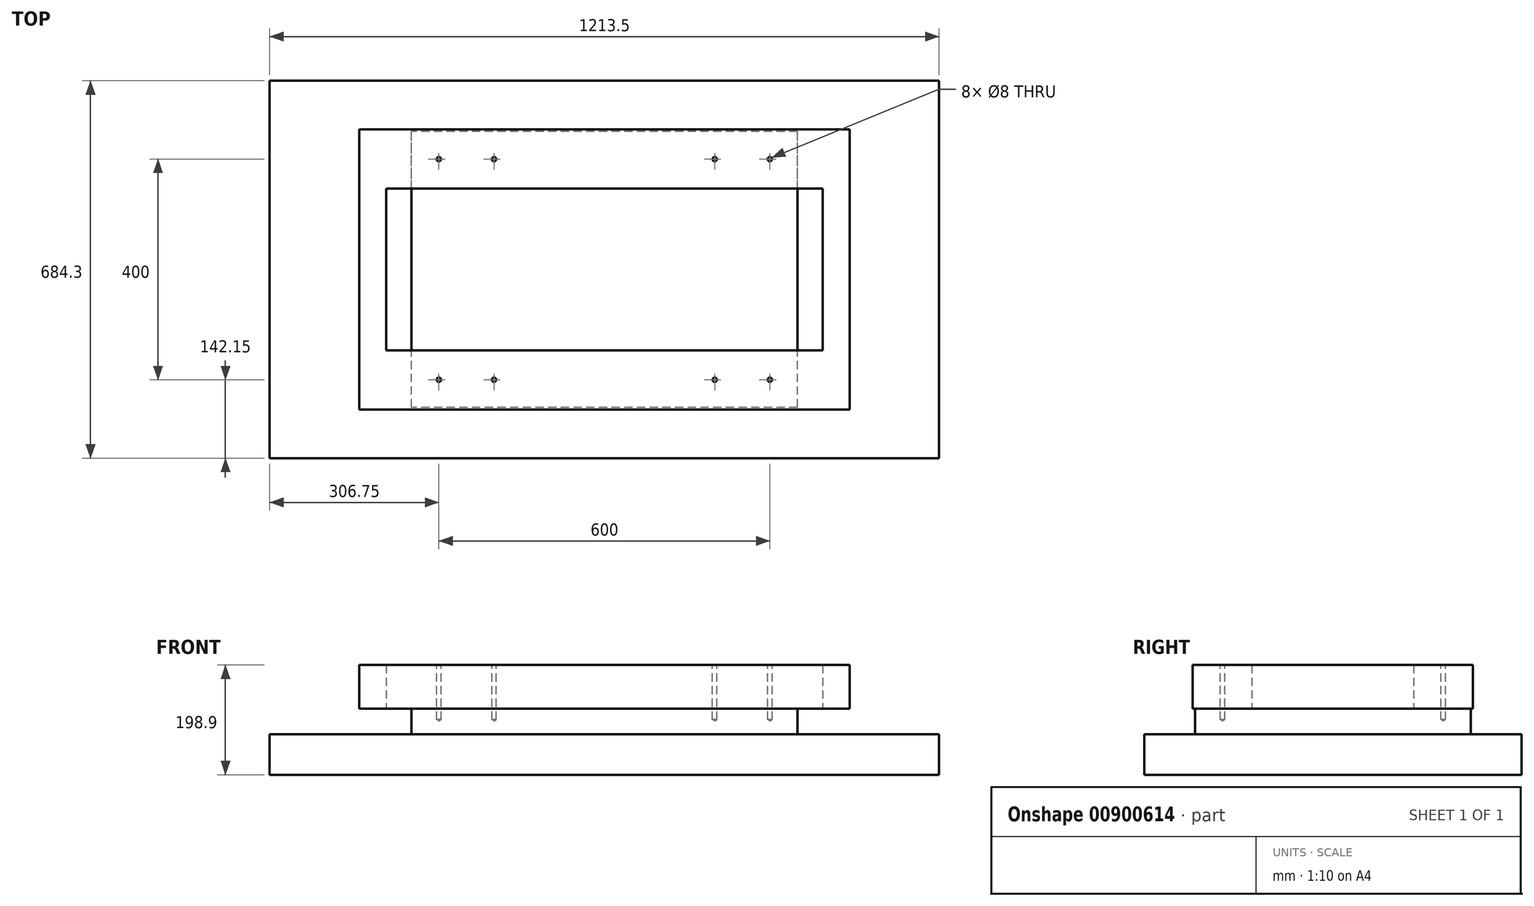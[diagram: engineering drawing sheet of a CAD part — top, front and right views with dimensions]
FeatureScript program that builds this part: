
annotation { "Feature Type Name" : "Feature", "Feature Type Description" : "" }
export const myFeature = defineFeature(function(context is Context, id is Id, definition is map)
    precondition{}
    {
        {
            var Q0;
            Q0=qCreatedBy(makeId("Top.planeOp"),FACE);
            var sketch = newSketch(context, id + "F0", { "sketchPlane" : qUnion([Q0])});
            skLineSegment(sketch, "E0.bottom", {"start": v(606.75, -342.15) * mm, "end": v(-606.75, -342.15) * mm});
            skLineSegment(sketch, "E0.top", {"start": v(606.75, 342.15) * mm, "end": v(-606.75, 342.15) * mm});
            skLineSegment(sketch, "E0.left", {"start": v(606.75, -342.15) * mm, "end": v(606.75, 342.15) * mm});
            skLineSegment(sketch, "E0.right", {"start": v(-606.75, -342.15) * mm, "end": v(-606.75, 342.15) * mm});
            skPoint(sketch, "E0.middle", {"position": v(0, 0) * mm});
            skSolve(sketch);
        }
        {
            var Q0;
            Q0=makeQuery(id+"F0.imprint","IMPRINT",FACE,{"disambiguationData":[TD([[makeQuery(id+"F0.imprint","IMPRINT",EDGE,{"derivedFrom":sQuery(id+"F0.wireOp",EDGE,"E0.bottom")}),-1.0]])]});
            extrude(context, id + "F1", {"entities" : qUnion([Q0]), "depth" : 73.4 * mm, "offsetDistance" : 25 * mm});
        }
        {
            var Q0;
            Q0=makeQuery(id+"F1.opExtrude","CAP_FACE",FACE,{"disambiguationData":[OSD([sQuery(id+"F0.wireOp",EDGE,"E0.bottom"),sQuery(id+"F0.wireOp",EDGE,"E0.top"),sQuery(id+"F0.wireOp",EDGE,"E0.left"),sQuery(id+"F0.wireOp",EDGE,"E0.right")])],"isStart":false});
            var sketch = newSketch(context, id + "F2", { "sketchPlane" : qUnion([Q0])});
            skLineSegment(sketch, "E1.bottom", {"start": v(350, -250) * mm, "end": v(-350, -250) * mm});
            skLineSegment(sketch, "E1.top", {"start": v(350, 250) * mm, "end": v(-350, 250) * mm});
            skLineSegment(sketch, "E1.left", {"start": v(350, -250) * mm, "end": v(350, 250) * mm});
            skLineSegment(sketch, "E1.right", {"start": v(-350, -250) * mm, "end": v(-350, 250) * mm});
            skPoint(sketch, "E1.middle", {"position": v(0, 0) * mm});
            skSolve(sketch);
        }
        {
            var Q0;
            Q0=makeQuery(id+"F2.imprint","IMPRINT",FACE,{"disambiguationData":[TD([[makeQuery(id+"F2.imprint","IMPRINT",EDGE,{"derivedFrom":sQuery(id+"F2.wireOp",EDGE,"E1.bottom")}),-1.0]])]});
            extrude(context, id + "F3", {"entities" : qUnion([Q0]), "operationType" : NewBodyOperationType.ADD, "depth" : 46.5 * mm, "offsetDistance" : 25 * mm});
        }
        {
            var Q0;
            Q0=makeQuery(id+"F3.opExtrude","CAP_FACE",FACE,{"disambiguationData":[OSD([sQuery(id+"F2.wireOp",EDGE,"E1.bottom"),sQuery(id+"F2.wireOp",EDGE,"E1.top"),sQuery(id+"F2.wireOp",EDGE,"E1.left"),sQuery(id+"F2.wireOp",EDGE,"E1.right")])],"isStart":false});
            var sketch = newSketch(context, id + "F4", { "sketchPlane" : qUnion([Q0])});
            skLineSegment(sketch, "E2.bottom", {"start": v(300, -200) * mm, "end": v(-300, -200) * mm});
            skLineSegment(sketch, "E2.top", {"start": v(300, 200) * mm, "end": v(-300, 200) * mm});
            skLineSegment(sketch, "E2.left", {"start": v(300, -200) * mm, "end": v(300, 200) * mm});
            skLineSegment(sketch, "E2.right", {"start": v(-300, -200) * mm, "end": v(-300, 200) * mm});
            skPoint(sketch, "E2.middle", {"position": v(0, 0) * mm});
            skLineSegment(sketch, "E3.bottom", {"start": v(200, -200) * mm, "end": v(-200, -200) * mm});
            skLineSegment(sketch, "E3.top", {"start": v(200, 200) * mm, "end": v(-200, 200) * mm});
            skLineSegment(sketch, "E3.left", {"start": v(200, -200) * mm, "end": v(200, 200) * mm});
            skLineSegment(sketch, "E3.right", {"start": v(-200, -200) * mm, "end": v(-200, 200) * mm});
            skCircle(sketch, "E4", {"center": v(-300, 200) * mm, "radius": 4 * mm});
            skCircle(sketch, "E5", {"center": v(-200, 200) * mm, "radius": 4 * mm});
            skCircle(sketch, "E6", {"center": v(200, 200) * mm, "radius": 4 * mm});
            skCircle(sketch, "E7", {"center": v(300, 200) * mm, "radius": 4 * mm});
            skCircle(sketch, "E8", {"center": v(-300, -200) * mm, "radius": 4 * mm});
            skCircle(sketch, "E9", {"center": v(-200, -200) * mm, "radius": 4 * mm});
            skCircle(sketch, "E10", {"center": v(200, -200) * mm, "radius": 4 * mm});
            skCircle(sketch, "E11", {"center": v(300, -200) * mm, "radius": 4 * mm});
            skSolve(sketch);
        }
        {
            var Q0;
            Q0=sQuery(id+"F4.wireOp",VERTEX,"E2.top.end");
            var Q1;
            Q1=sQuery(id+"F4.wireOp",VERTEX,"E3.top.end");
            var Q2;
            Q2=sQuery(id+"F4.wireOp",VERTEX,"E3.top.start");
            var Q3;
            Q3=sQuery(id+"F4.wireOp",VERTEX,"E2.top.start");
            var Q4;
            Q4=sQuery(id+"F4.wireOp",VERTEX,"E2.bottom.start");
            var Q5;
            Q5=sQuery(id+"F4.wireOp",VERTEX,"E3.bottom.start");
            var Q6;
            Q6=sQuery(id+"F4.wireOp",VERTEX,"E3.bottom.end");
            var Q7;
            Q7=sQuery(id+"F4.wireOp",VERTEX,"E2.bottom.end");
            var Q8;
            Q8=makeQuery(id+"F1.opExtrude","SWEPT_BODY",BODY,{"disambiguationData":[OSD([sQuery(id+"F0.wireOp",EDGE,"E0.bottom"),sQuery(id+"F0.wireOp",EDGE,"E0.top"),sQuery(id+"F0.wireOp",EDGE,"E0.left"),sQuery(id+"F0.wireOp",EDGE,"E0.right")])]});
            hole(context, id + "F5", {"style" : HoleStyle.SIMPLE, "endStyle" : HoleEndStyle.BLIND, "holeDiameter" : 8 * mm, "majorDiameter" : 5 * mm, "holeDepth" : 20 * mm, "isTappedThrough" : true, "tappedDepth" : 12 * mm, "tapClearance" : 3, "locations" : qUnion([Q0, Q1, Q2, Q3, Q4, Q5, Q6, Q7]), "scope" : qUnion([Q8])});
        }
        {
            var Q0;
            Q0=makeQuery(id+"F3.opExtrude","CAP_FACE",FACE,{"disambiguationData":[OSD([sQuery(id+"F2.wireOp",EDGE,"E1.bottom"),sQuery(id+"F2.wireOp",EDGE,"E1.top"),sQuery(id+"F2.wireOp",EDGE,"E1.left"),sQuery(id+"F2.wireOp",EDGE,"E1.right")])],"isStart":false});
            var sketch = newSketch(context, id + "F6", { "sketchPlane" : qUnion([Q0])});
            skLineSegment(sketch, "E12.bottom", {"start": v(444.5, -254) * mm, "end": v(-444.5, -254) * mm});
            skLineSegment(sketch, "E12.top", {"start": v(444.5, 254) * mm, "end": v(-444.5, 254) * mm});
            skLineSegment(sketch, "E12.left", {"start": v(444.5, -254) * mm, "end": v(444.5, 254) * mm});
            skLineSegment(sketch, "E12.right", {"start": v(-444.5, -254) * mm, "end": v(-444.5, 254) * mm});
            skPoint(sketch, "E12.middle", {"position": v(0, 0) * mm});
            skLineSegment(sketch, "E13.0.0", {"start": v(350, -250) * mm, "end": v(350, 250) * mm});
            skLineSegment(sketch, "E13.0.1", {"start": v(350, 250) * mm, "end": v(-350, 250) * mm});
            skLineSegment(sketch, "E13.0.2", {"start": v(-350, 250) * mm, "end": v(-350, -250) * mm});
            skLineSegment(sketch, "E13.0.3", {"start": v(-350, -250) * mm, "end": v(350, -250) * mm});
            skCircle(sketch, "E14.0", {"center": v(-300, 200) * mm, "radius": 4 * mm});
            skPoint(sketch, "E15.0", {"position": v(-300, -200) * mm});
            skCircle(sketch, "E16.0", {"center": v(-300, -200) * mm, "radius": 4 * mm});
            skCircle(sketch, "E17.0", {"center": v(200, -200) * mm, "radius": 4 * mm});
            skCircle(sketch, "E18.0", {"center": v(200, 200) * mm, "radius": 4 * mm});
            skLineSegment(sketch, "E19.bottom", {"start": v(-395.68, -146.73) * mm, "end": v(395.68, -146.73) * mm});
            skLineSegment(sketch, "E19.top", {"start": v(-395.68, 146.73) * mm, "end": v(395.68, 146.73) * mm});
            skLineSegment(sketch, "E19.left", {"start": v(-395.68, -146.73) * mm, "end": v(-395.68, 146.73) * mm});
            skLineSegment(sketch, "E19.right", {"start": v(395.68, -146.73) * mm, "end": v(395.68, 146.73) * mm});
            skSolve(sketch);
        }
        {
            var Q0;
            Q0=makeQuery(id+"F6.imprint","IMPRINT",FACE,{"disambiguationData":[TD([[makeQuery(id+"F6.imprint","IMPRINT",EDGE,{"derivedFrom":sQuery(id+"F6.wireOp",EDGE,"E12.bottom")}),-1.0]])]});
            var Q1;
            {var subQ1=sQuery(id+"F6.wireOp",EDGE,"E13.0.1");Q1=makeQuery(id+"F6.imprint","IMPRINT",FACE,{"disambiguationData":[TD([[makeQuery(id+"F6.imprint","IMPRINT",EDGE,{"derivedFrom":subQ1}),1.0]])]});}
            var Q2;
            {var subQ0=sQuery(id+"F6.wireOp",EDGE,"E13.0.3");Q2=makeQuery(id+"F6.imprint","IMPRINT",FACE,{"disambiguationData":[TD([[makeQuery(id+"F6.imprint","IMPRINT",EDGE,{"derivedFrom":subQ0}),-1.0]])]});}
            extrude(context, id + "F7", {"entities" : qUnion([Q0, Q1, Q2]), "operationType" : NewBodyOperationType.ADD, "depth" : 79 * mm, "offsetDistance" : 25 * mm});
        }
    });
